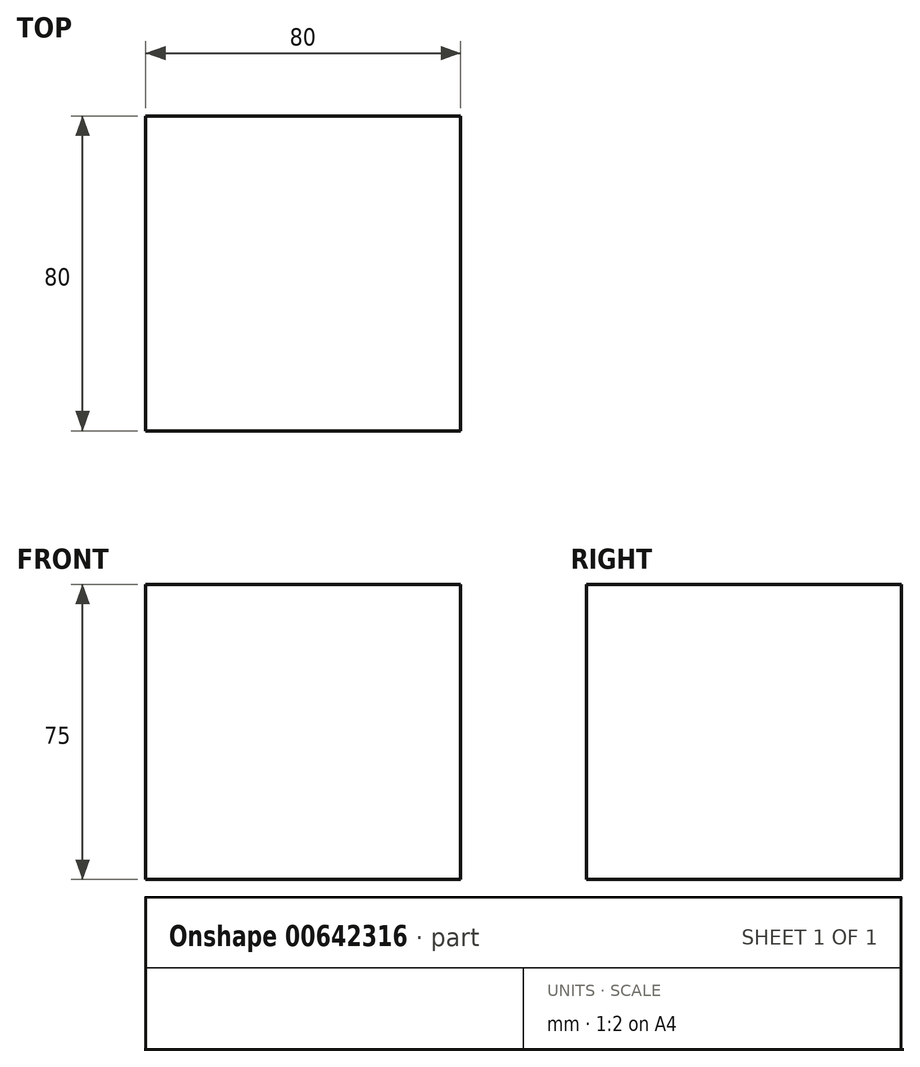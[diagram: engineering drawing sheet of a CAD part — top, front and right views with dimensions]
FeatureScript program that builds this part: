
annotation { "Feature Type Name" : "Feature", "Feature Type Description" : "" }
export const myFeature = defineFeature(function(context is Context, id is Id, definition is map)
    precondition{}
    {
        {
            var Q0;
            Q0=qCreatedBy(makeId("Top.planeOp"),FACE);
            var sketch = newSketch(context, id + "F0", { "sketchPlane" : qUnion([Q0])});
            skLineSegment(sketch, "E0.bottom", {"start": v(40, -40) * mm, "end": v(-40, -40) * mm});
            skLineSegment(sketch, "E0.top", {"start": v(40, 40) * mm, "end": v(-40, 40) * mm});
            skLineSegment(sketch, "E0.left", {"start": v(40, -40) * mm, "end": v(40, 40) * mm});
            skLineSegment(sketch, "E0.right", {"start": v(-40, -40) * mm, "end": v(-40, 40) * mm});
            skPoint(sketch, "E0.middle", {"position": v(0, 0) * mm});
            skSolve(sketch);
        }
        {
            var Q0;
            Q0=makeQuery(id+"F0.imprint","IMPRINT",FACE,{"disambiguationData":[TD([[makeQuery(id+"F0.imprint","IMPRINT",EDGE,{"derivedFrom":sQuery(id+"F0.wireOp",EDGE,"E0.bottom")}),-1.0]])]});
            extrude(context, id + "F1", {"entities" : qUnion([Q0]), "depth" : 75 * mm, "offsetDistance" : 25 * mm});
        }
    });
